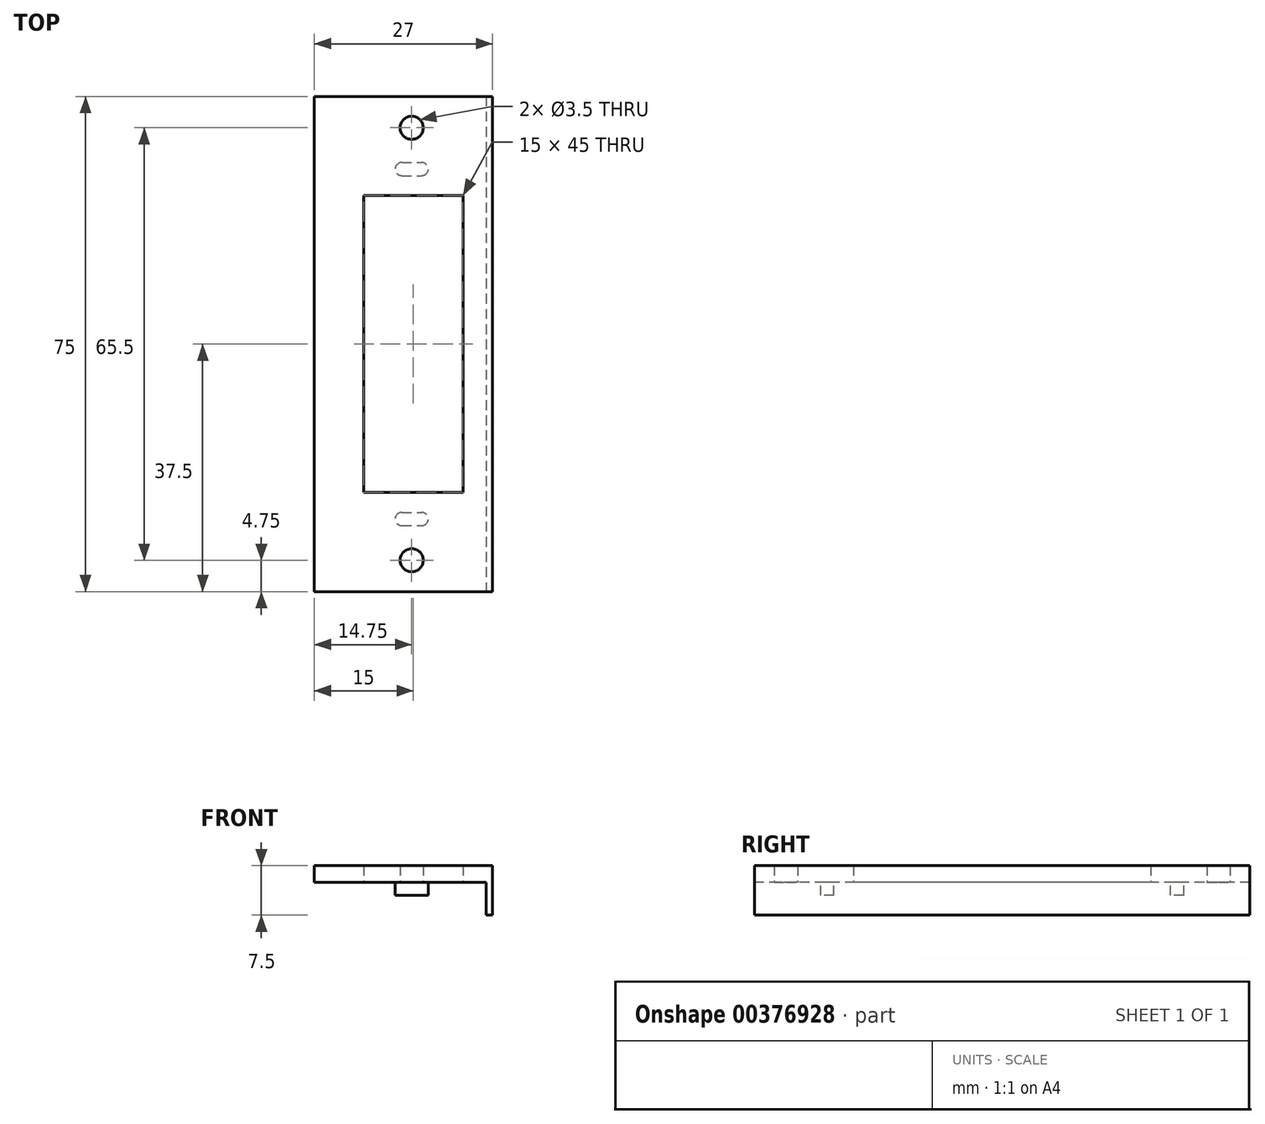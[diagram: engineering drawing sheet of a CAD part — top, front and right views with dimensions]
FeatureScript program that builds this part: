
annotation { "Feature Type Name" : "Feature", "Feature Type Description" : "" }
export const myFeature = defineFeature(function(context is Context, id is Id, definition is map)
    precondition{}
    {
        {
            assignVariable(context, id + "F0", {"name" : "diktePlaat", "anyValue" : 2.5 * mm});
        }
        {
            var Q0;
            Q0=qCreatedBy(makeId("Top.planeOp"),FACE);
            var sketch = newSketch(context, id + "F1", { "sketchPlane" : qUnion([Q0])});
            skLineSegment(sketch, "E0", {"start": v(0, 40.8) * mm, "end": v(0, -40.84) * mm, "construction": true});
            skLineSegment(sketch, "E1", {"start": v(-24.9, 0) * mm, "end": v(24.74, 0) * mm, "construction": true});
            skLineSegment(sketch, "E2.bottom", {"start": v(7.75, 22.5) * mm, "end": v(-7.25, 22.5) * mm});
            skLineSegment(sketch, "E2.top", {"start": v(7.75, -22.5) * mm, "end": v(-7.25, -22.5) * mm});
            skLineSegment(sketch, "E2.left", {"start": v(7.75, 22.5) * mm, "end": v(7.75, -22.5) * mm});
            skLineSegment(sketch, "E2.right", {"start": v(-7.25, 22.5) * mm, "end": v(-7.25, -22.5) * mm});
            skPoint(sketch, "E2.middle", {"position": v(0, 0) * mm});
            skLineSegment(sketch, "E3.bottom", {"start": v(12.25, 37.5) * mm, "end": v(-14.75, 37.5) * mm});
            skLineSegment(sketch, "E3.top", {"start": v(12.25, -37.5) * mm, "end": v(-14.75, -37.5) * mm});
            skLineSegment(sketch, "E3.left", {"start": v(12.25, 37.5) * mm, "end": v(12.25, -37.5) * mm});
            skLineSegment(sketch, "E3.right", {"start": v(-14.75, 37.5) * mm, "end": v(-14.75, -37.5) * mm});
            skLineSegment(sketch, "E4", {"start": v(-19.08, 32.75) * mm, "end": v(18.92, 32.75) * mm, "construction": true});
            skLineSegment(sketch, "E5.MirrorCS", {"start": v(-19.08, -32.75) * mm, "end": v(18.92, -32.75) * mm, "construction": true});
            skCircle(sketch, "E6", {"center": v(0, 32.75) * mm, "radius": 1.75 * mm});
            skCircle(sketch, "E7.MirrorC", {"center": v(0, -32.75) * mm, "radius": 1.75 * mm});
            skSolve(sketch);
        }
        {
            var Q0;
            Q0=makeQuery(id+"F1.imprint","IMPRINT",FACE,{"disambiguationData":[TD([[makeQuery(id+"F1.imprint","IMPRINT",EDGE,{"derivedFrom":sQuery(id+"F1.wireOp",EDGE,"E2.bottom")}),-1.0]])]});
            extrude(context, id + "F2", {"entities" : qUnion([Q0]), "depth" : getVariable(context, 'diktePlaat')});
        }
        {
            var Q0;
            Q0=makeQuery(id+"F2.opExtrude","SWEPT_FACE",FACE,{"disambiguationData":[OSD([sQuery(id+"F1.wireOp",EDGE,"E3.left")])]});
            var sketch = newSketch(context, id + "F3", { "sketchPlane" : qUnion([Q0])});
            skLineSegment(sketch, "E8", {"start": v(37.5, 0) * mm, "end": v(37.5, -5) * mm});
            skLineSegment(sketch, "E9", {"start": v(37.5, -5) * mm, "end": v(-37.5, -5) * mm});
            skLineSegment(sketch, "E10", {"start": v(-37.5, -5) * mm, "end": v(-37.5, 0) * mm});
            skSolve(sketch);
        }
        {
            var Q0;
            Q0=makeQuery(id+"F3.imprint","IMPRINT",FACE,{"disambiguationData":[TD([[makeQuery(id+"F3.imprint","IMPRINT",EDGE,{"derivedFrom":sQuery(id+"F3.wireOp",EDGE,"E8")}),-1.0]])]});
            extrude(context, id + "F4", {"entities" : qUnion([Q0]), "operationType" : NewBodyOperationType.ADD, "oppositeDirection" : true, "depth" : 1 * mm});
        }
        {
            var Q0;
            Q0=makeQuery(id+"F2.opExtrude","CAP_FACE",FACE,{"disambiguationData":[OSD([sQuery(id+"F1.wireOp",EDGE,"E2.bottom"),sQuery(id+"F1.wireOp",EDGE,"E2.top"),sQuery(id+"F1.wireOp",EDGE,"E2.left"),sQuery(id+"F1.wireOp",EDGE,"E2.right"),sQuery(id+"F1.wireOp",EDGE,"E3.bottom"),sQuery(id+"F1.wireOp",EDGE,"E3.top"),sQuery(id+"F1.wireOp",EDGE,"E3.left"),sQuery(id+"F1.wireOp",EDGE,"E3.right"),sQuery(id+"F1.wireOp",EDGE,"E6"),sQuery(id+"F1.wireOp",EDGE,"E7.MirrorC")])],"isStart":true});
            var sketch = newSketch(context, id + "F5", { "sketchPlane" : qUnion([Q0])});
            skLineSegment(sketch, "E11", {"start": v(0, -46.02) * mm, "end": v(0, 45.5) * mm, "construction": true});
            skPoint(sketch, "E12.orphan", {"position": v(0, -32.75) * mm});
            skPoint(sketch, "E13.orphan", {"position": v(0, 32.75) * mm});
            skLineSegment(sketch, "E14", {"start": v(-18.02, 0) * mm, "end": v(16.37, 0) * mm, "construction": true});
            skLineSegment(sketch, "E15.bottom", {"start": v(-1.5, 27.5) * mm, "end": v(1.5, 27.5) * mm});
            skLineSegment(sketch, "E15.top", {"start": v(-1.5, 25.5) * mm, "end": v(1.5, 25.5) * mm});
            skLineSegment(sketch, "E15.left", {"start": v(-2.5, 26.5) * mm, "end": v(-2.5, 26.5) * mm});
            skLineSegment(sketch, "E15.right", {"start": v(2.5, 26.5) * mm, "end": v(2.5, 26.5) * mm});
            skLineSegment(sketch, "E16.MirrorCS", {"start": v(2.5, -26.5) * mm, "end": v(2.5, -26.5) * mm});
            skLineSegment(sketch, "E17.MirrorCS", {"start": v(-2.5, -26.5) * mm, "end": v(-2.5, -26.5) * mm});
            skLineSegment(sketch, "E18.MirrorCS", {"start": v(-1.5, -27.5) * mm, "end": v(1.5, -27.5) * mm});
            skLineSegment(sketch, "E19.MirrorCS", {"start": v(-1.5, -25.5) * mm, "end": v(1.5, -25.5) * mm});
            skPoint(sketch, "E20.visualSharp", {"position": v(2.5, 27.5) * mm});
            skArc(sketch, "E20.filletArc", {"start": v(2.5, 26.5) * mm, "mid": v(2.2, 27.2) * mm, "end": v(1.5, 27.5) * mm});
            skPoint(sketch, "E21.visualSharp", {"position": v(2.5, 25.5) * mm});
            skArc(sketch, "E21.filletArc", {"start": v(1.5, 25.5) * mm, "mid": v(2.2, 25.8) * mm, "end": v(2.5, 26.5) * mm});
            skPoint(sketch, "E22.visualSharp", {"position": v(-2.5, 25.5) * mm});
            skArc(sketch, "E22.filletArc", {"start": v(-2.5, 26.5) * mm, "mid": v(-2.2, 25.8) * mm, "end": v(-1.5, 25.5) * mm});
            skPoint(sketch, "E23.visualSharp", {"position": v(-2.5, 27.5) * mm});
            skArc(sketch, "E23.filletArc", {"start": v(-1.5, 27.5) * mm, "mid": v(-2.2, 27.2) * mm, "end": v(-2.5, 26.5) * mm});
            skPoint(sketch, "E24.visualSharp", {"position": v(2.5, -25.5) * mm});
            skArc(sketch, "E24.filletArc", {"start": v(2.5, -26.5) * mm, "mid": v(2.2, -25.8) * mm, "end": v(1.5, -25.5) * mm});
            skPoint(sketch, "E25.visualSharp", {"position": v(2.5, -27.5) * mm});
            skArc(sketch, "E25.filletArc", {"start": v(1.5, -27.5) * mm, "mid": v(2.2, -27.2) * mm, "end": v(2.5, -26.5) * mm});
            skPoint(sketch, "E26.visualSharp", {"position": v(-2.5, -27.5) * mm});
            skArc(sketch, "E26.filletArc", {"start": v(-2.5, -26.5) * mm, "mid": v(-2.2, -27.2) * mm, "end": v(-1.5, -27.5) * mm});
            skPoint(sketch, "E27.visualSharp", {"position": v(-2.5, -25.5) * mm});
            skArc(sketch, "E27.filletArc", {"start": v(-1.5, -25.5) * mm, "mid": v(-2.2, -25.8) * mm, "end": v(-2.5, -26.5) * mm});
            skSolve(sketch);
        }
        {
            var Q0;
            Q0=makeQuery(id+"F5.imprint","IMPRINT",FACE,{"disambiguationData":[TD([[makeQuery(id+"F5.imprint","IMPRINT",EDGE,{"derivedFrom":sQuery(id+"F5.wireOp",EDGE,"E15.bottom")}),-1.0]])]});
            var Q1;
            Q1=makeQuery(id+"F5.imprint","IMPRINT",FACE,{"disambiguationData":[TD([[makeQuery(id+"F5.imprint","IMPRINT",EDGE,{"derivedFrom":sQuery(id+"F5.wireOp",EDGE,"E18.MirrorCS")}),1.0]])]});
            extrude(context, id + "F6", {"entities" : qUnion([Q0, Q1]), "operationType" : NewBodyOperationType.ADD, "depth" : 2 * mm});
        }
    });
